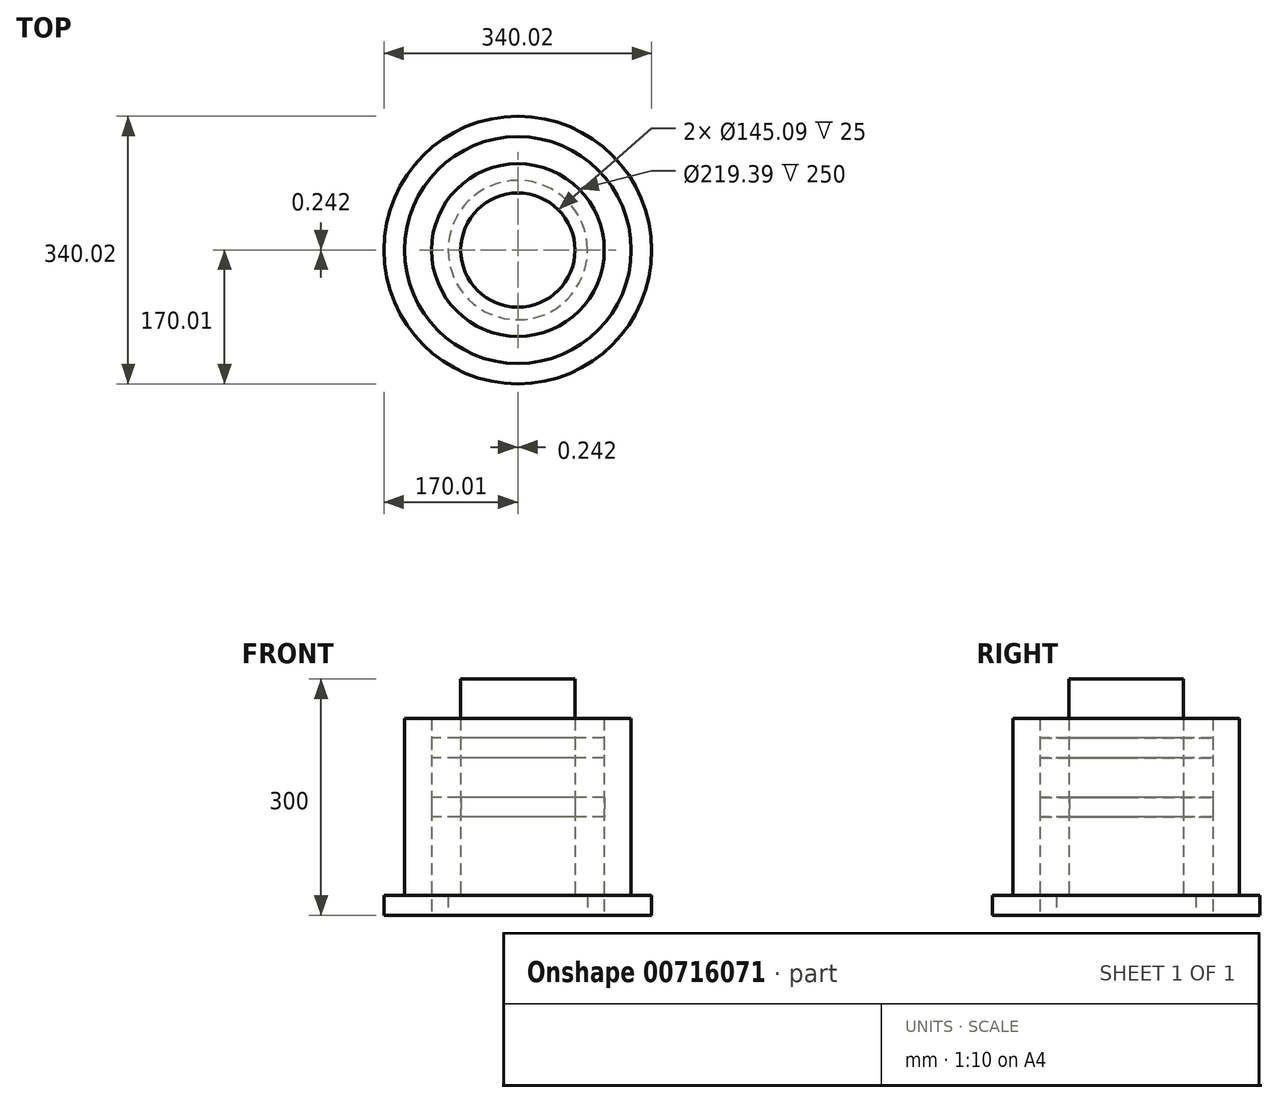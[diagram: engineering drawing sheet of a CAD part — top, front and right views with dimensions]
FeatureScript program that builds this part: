
annotation { "Feature Type Name" : "Feature", "Feature Type Description" : "" }
export const myFeature = defineFeature(function(context is Context, id is Id, definition is map)
    precondition{}
    {
        {
            var Q0;
            Q0=qCreatedBy(makeId("Top.planeOp"),FACE);
            var sketch = newSketch(context, id + "F0", { "sketchPlane" : qUnion([Q0])});
            skCircle(sketch, "E0", {"center": v(0, 0) * mm, "radius": 170.01 * mm});
            skCircle(sketch, "E1", {"center": v(0, 0) * mm, "radius": 143.98 * mm});
            skCircle(sketch, "E2", {"center": v(0, 0) * mm, "radius": 109.7 * mm});
            skCircle(sketch, "E3", {"center": v(0, 0) * mm, "radius": 88.5 * mm});
            skCircle(sketch, "E4", {"center": v(0, 0) * mm, "radius": 72.54 * mm});
            skSolve(sketch);
        }
        {
            var Q0;
            Q0=makeQuery(id+"F0.imprint","IMPRINT",FACE,{"disambiguationData":[TD([[makeQuery(id+"F0.imprint","IMPRINT",EDGE,{"derivedFrom":sQuery(id+"F0.wireOp",EDGE,"E0")}),1.0]])]});
            extrude(context, id + "F1", {"entities" : qUnion([Q0]), "depth" : 25 * mm, "offsetDistance" : 25 * mm});
        }
        {
            var Q0;
            Q0=makeQuery(id+"F0.imprint","IMPRINT",FACE,{"disambiguationData":[TD([[makeQuery(id+"F0.imprint","IMPRINT",EDGE,{"derivedFrom":sQuery(id+"F0.wireOp",EDGE,"E1")}),1.0]])]});
            extrude(context, id + "F2", {"entities" : qUnion([Q0]), "operationType" : NewBodyOperationType.ADD, "depth" : 250 * mm, "offsetDistance" : 25 * mm});
        }
        {
            var Q0;
            Q0=makeQuery(id+"F0.imprint","IMPRINT",FACE,{"disambiguationData":[TD([[makeQuery(id+"F0.imprint","IMPRINT",EDGE,{"derivedFrom":sQuery(id+"F0.wireOp",EDGE,"E4")}),1.0]])]});
            extrude(context, id + "F3", {"entities" : qUnion([Q0]), "depth" : 300 * mm, "offsetDistance" : 25 * mm});
        }
        {
            var Q0;
            Q0=makeQuery(id+"F0.imprint","IMPRINT",FACE,{"disambiguationData":[TD([[makeQuery(id+"F0.imprint","IMPRINT",EDGE,{"derivedFrom":sQuery(id+"F0.wireOp",EDGE,"E3")}),1.0]])]});
            extrude(context, id + "F4", {"entities" : qUnion([Q0]), "operationType" : NewBodyOperationType.ADD, "depth" : 25 * mm, "offsetDistance" : 25 * mm});
        }
        {
            var Q0;
            Q0=makeQuery(id+"F1.opExtrude","CAP_FACE",FACE,{"disambiguationData":[OSD([sQuery(id+"F0.wireOp",EDGE,"E0"),sQuery(id+"F0.wireOp",EDGE,"E1")])],"isStart":false});
            cPlane(context, id + "F5", {"entities" : qUnion([Q0]), "cplaneType" : CPlaneType.OFFSET, "offset" : 100 * mm, "width" : 150 * mm, "height" : 150 * mm});
        }
        {
            var Q0;
            Q0=makeQuery(id+"F1.opExtrude","CAP_FACE",FACE,{"disambiguationData":[OSD([sQuery(id+"F0.wireOp",EDGE,"E0"),sQuery(id+"F0.wireOp",EDGE,"E1")])],"isStart":false});
            cPlane(context, id + "F6", {"entities" : qUnion([Q0]), "cplaneType" : CPlaneType.OFFSET, "offset" : 175 * mm, "width" : 150 * mm, "height" : 150 * mm});
        }
        {
            var Q0;
            Q0=qCreatedBy(id+"F5.planeOp",FACE);
            var sketch = newSketch(context, id + "F7", { "sketchPlane" : qUnion([Q0])});
            skCircle(sketch, "E5", {"center": v(0.24, 0.24) * mm, "radius": 109.7 * mm});
            skCircle(sketch, "E6", {"center": v(0.24, 0.24) * mm, "radius": 72.54 * mm});
            skSolve(sketch);
        }
        {
            var Q0;
            Q0=qCreatedBy(id+"F6.planeOp",FACE);
            var sketch = newSketch(context, id + "F8", { "sketchPlane" : qUnion([Q0])});
            skCircle(sketch, "E7", {"center": v(0, 0) * mm, "radius": 109.7 * mm});
            skCircle(sketch, "E8", {"center": v(0, 0) * mm, "radius": 72.54 * mm});
            skSolve(sketch);
        }
        {
            var Q0;
            Q0 = qSketchRegion(id + "F7", true);
            var Q1;
            Q1 = qSketchRegion(id + "F8", true);
            extrude(context, id + "F9", {"entities" : qUnion([Q0, Q1]), "depth" : 25 * mm, "offsetDistance" : 25 * mm});
        }
    });
